# Revit family: ALBA_R100ExSWxx
name_source: partatom
category: Leuchten
units: mm (PartAtom-declared; Revit-internal decimal feet)

## family parameters
Basisbauteil = Fläche
Beim Laden mit Abzugskörper schneiden = Nein
Bemaßung runder Anschluss = Durchmesser verwenden
Gemeinsam genutzt = Nein
Lichtquelle = Ja
OmniClass-Nummer = 23.80.70.11
OmniClass-Titel = Luminaries for Internal Lighting
Raumberechnungspunkt = Nein
Teiletyp = Normal

## types (12) — shared parameters
Baugruppenkennzeichen = D5020200
Emissionsform beim Rendern sichtbar = Nein
Farbfilter = 16777215
Farbtemperaturverschiebung bei Dämpfen der Lampe = <Keine Auswahl>
Hersteller = RIDI Leuchten GmbH
Lampe = LED
Neigungswinkel = 90.00°
Scheinlast = 15 VA
URL = www.ridi.de
Von Kreisdurchmesser aussenden = 86 mm  [stored 0.282152 ft]
brand = RIDI
conformity mark = CE
electrical safety class = 2
height = 84 mm  [stored 0.275591 ft]
ingress protection (IP) code = IP20
length = 112 mm  [stored 0.367454 ft]
nominal frequency = 50-60Hz
nominal voltage = 230
rated input power = 15
voltage type (AC, DC, UC) = AC
weight = 0.43 kg
width = 112 mm  [stored 0.367454 ft]
zero-valued in all types: Vorgabe-Ansicht

## per-type parameters (varying)
| type | Datei für fotometrisches Netz | Modell |
| ALBA R100E NDSW930SF0150OS | Master_ALBA_R100E_NDSW840_Diffusor.IES | 0322123 |
| ALBA R100E NDSW940SF0150OS | Master_ALBA_R100E_NDSW840_Diffusor.IES | 0322124 |
| ALBA R100E NDSW930M0150 | Master_ALBA_R100E_NDSW840_Linse_M.IES | 0322125 |
| ALBA R100E NDSW940M0150 | Master_ALBA_R100E_NDSW840_Linse_M.IES | 0322126 |
| ALBA R100E DASW930SF0150OS | Master_ALBA_R100E_NDSW840_Diffusor.IES | 0332123 |
| ALBA R100E DASW940SF0150OS | Master_ALBA_R100E_NDSW840_Diffusor.IES | 0332124 |
| ALBA R100E DASW930M0150 | Master_ALBA_R100E_NDSW840_Linse_M.IES | 0332125 |
| ALBA R100E DASW940M0150 | Master_ALBA_R100E_NDSW840_Linse_M.IES | 0332126 |
| ALBA R100E NDSW930S0150J | Master_ALBA_R100E_NDSW840_Linse_M.IES | 0322127 |
| ALBA R100E NDSW940S0150J | Master_ALBA_R100E_NDSW840_Linse_M.IES | 0322128 |
| ALBA R100E DASW930S0150J | Master_ALBA_R100E_NDSW840_Linse_M.IES | 0332127 |
| ALBA R100E DASW940S0150J | Master_ALBA_R100E_NDSW840_Linse_M.IES | 0332128 |

note: column(s) folded — value = type name in every type: product name

note: [stored X ft] marks values corroborated as IEEE doubles in the binary element streams (Revit-internal decimal feet)
